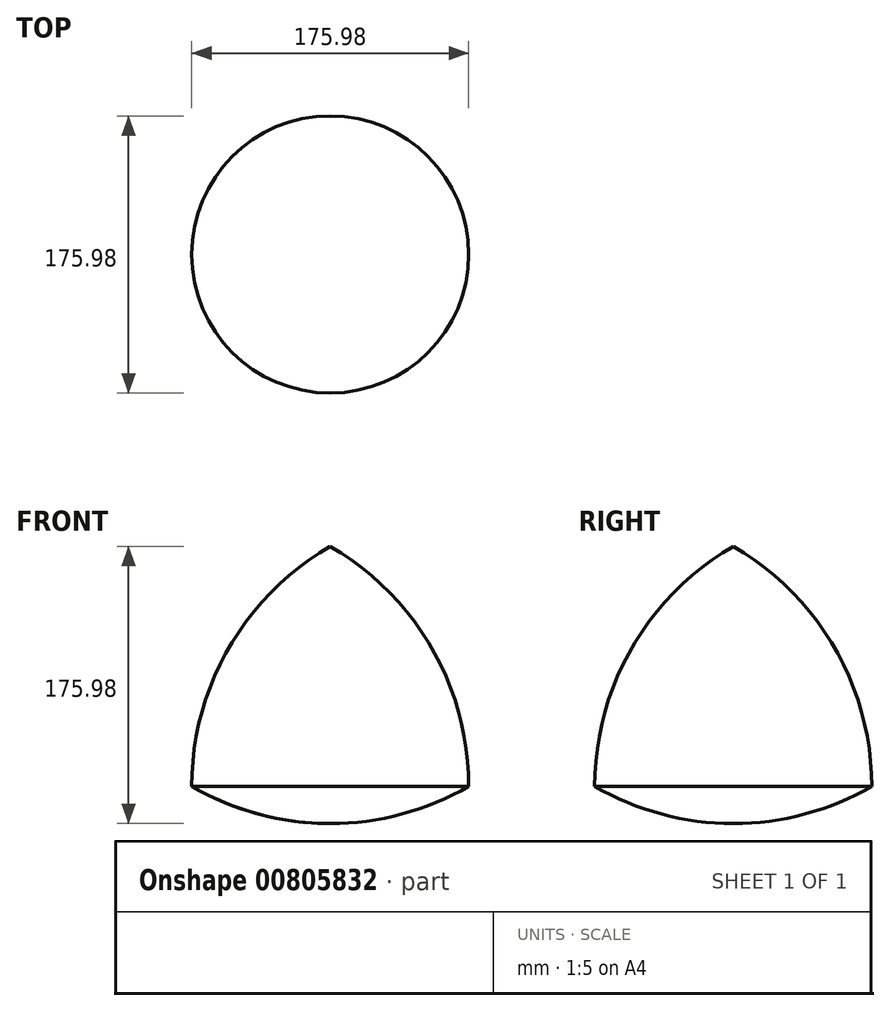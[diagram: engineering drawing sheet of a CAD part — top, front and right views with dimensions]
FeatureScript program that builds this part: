
annotation { "Feature Type Name" : "Feature", "Feature Type Description" : "" }
export const myFeature = defineFeature(function(context is Context, id is Id, definition is map)
    precondition{}
    {
        {
            var Q0;
            Q0=qCreatedBy(makeId("Front.planeOp"),FACE);
            var sketch = newSketch(context, id + "F0", { "sketchPlane" : qUnion([Q0])});
            skCircle(sketch, "E0.cCircle", {"center": v(0, 0) * mm, "radius": 50.8 * mm, "construction": true});
            skLineSegment(sketch, "E0.0", {"start": v(0, 101.6) * mm, "end": v(87.99, -50.8) * mm});
            skLineSegment(sketch, "E0.1", {"start": v(87.99, -50.8) * mm, "end": v(-87.99, -50.8) * mm});
            skLineSegment(sketch, "E0.2", {"start": v(-87.99, -50.8) * mm, "end": v(0, 101.6) * mm});
            skPoint(sketch, "E0.0.midPoint", {"position": v(44, 25.4) * mm});
            skCircle(sketch, "E1", {"center": v(-87.99, -50.8) * mm, "radius": 175.98 * mm});
            skCircle(sketch, "E2", {"center": v(87.99, -50.8) * mm, "radius": 175.98 * mm});
            skCircle(sketch, "E3", {"center": v(0, 101.6) * mm, "radius": 175.98 * mm});
            skLineSegment(sketch, "E4", {"start": v(0, 127) * mm, "end": v(0, -101.6) * mm});
            skSolve(sketch);
        }
        {
            var Q0;
            {var subQ0=sQuery(id+"F0.wireOp",EDGE,"E0.0");Q0=makeQuery(id+"F0.imprint","IMPRINT",FACE,{"disambiguationData":[TD([[makeQuery(id+"F0.imprint","IMPRINT",EDGE,{"derivedFrom":subQ0}),-1.0]])]});}
            var Q1;
            {var subQ0=sQuery(id+"F0.wireOp",EDGE,"E0.0");Q1=makeQuery(id+"F0.imprint","IMPRINT",FACE,{"disambiguationData":[TD([[makeQuery(id+"F0.imprint","IMPRINT",EDGE,{"derivedFrom":subQ0}),1.0]])]});}
            var Q2;
            {var subQ0=sQuery(id+"F0.wireOp",EDGE,"E3");var subQ3=sQuery(id+"F0.wireOp",EDGE,"E4");var subQ5=makeQuery(id+"F0.imprint","INTERSECT",VERTEX,{"derivedFrom":[subQ0,subQ3]});Q2=makeQuery(id+"F0.imprint","IMPRINT",FACE,{"disambiguationData":[TD([[makeQuery(id+"F0.imprint","IMPRINT",EDGE,{"disambiguationData":[TD([[subQ5,1.0]])],"derivedFrom":subQ3}),1.0]])]});}
            var Q3;
            Q3=sQuery(id+"F0.wireOp",EDGE,"E0.2");
            var Q4;
            Q4=sQuery(id+"F0.wireOp",EDGE,"E4");
            revolve(context, id + "F1", {"surfaceOperationType" : NewSurfaceOperationType.NEW, "entities" : qUnion([Q0, Q1, Q2]), "surfaceEntities" : qUnion([Q3]), "axis" : qUnion([Q4]), "revolveType" : RevolveType.FULL});
        }
    });
